# Revit family: LQ4085551_Mezclador Monocontrol Liquid CD
name_source: partatom
category: Aparatos sanitarios
units: mm (PartAtom-declared; Revit-internal decimal feet)

## family parameters
Anfitrión = Muro
Compartido = No
Corte con vacíos al cargar = No
Cota de conector redondo = Diámetro de uso
Punto de cálculo de habitación = No
Siempre vertical = Sí
Tipo de pieza = Normal

## types (1)
- Type 1
    Alto = 164 mm
    Ancho = 140 mm
    Creado por = IDD
    Descripción = La línea de griferías, duchas y accesorios Liquid se inspira en la tensión superficial del agua
y en cómo esta crea formas armoniosas adaptándose al ambiente. Al igual que el agua,
las superficies de las griferías Liquid juegan con la luz y los reflejos que fluyen alrededor
de sus formas, sus líneas continuas y simplicidad formal proporcionan la ventaja práctica,
limpieza sin esfuerzo.
ŤCon Tecnología Duracrome: acabado superior, mayor espesor en el cromado que lo
hace más brillante y resistente a la corrosión.
ŤCon botón desviador: facilita la selección de salida de agua ya sea por la regadera,
la salida auxiliar para teleducha o salida a la bañera.
    Dimensiones generales del producto = (H x W x L): 164 x 140 x 133 mm.
(H x W x L): 6,5 x 5,5 x 5,2 pulg.
    Fabricante = Corona
    Fecha de creación = 28/07/2020
    Garantía = 30 años
    Garantía Acabados = 5 años
    Material = Corona_Metal
    Peso  Bruto = 1.190 g. - 2,62 lb.
    Peso neto = 910 g. - 2,01 lb.
    Presion maxima = 125 psi (860 Kpa).
    Presion minima = 20 psi (140 Kpa).
    Profundidad = 71 mm
    Temperaturas máxima de trabajo = 71°C / 159,8°F
    Temperaturas mínima de trabajo = 5°C / 41 °F
    Vida útil = 250.000 ciclos.

## geometry (parser evidence)
native form markers: Blend x3, Extrusion x1, Sweep x5
no freeform markers — native parametric forms only
